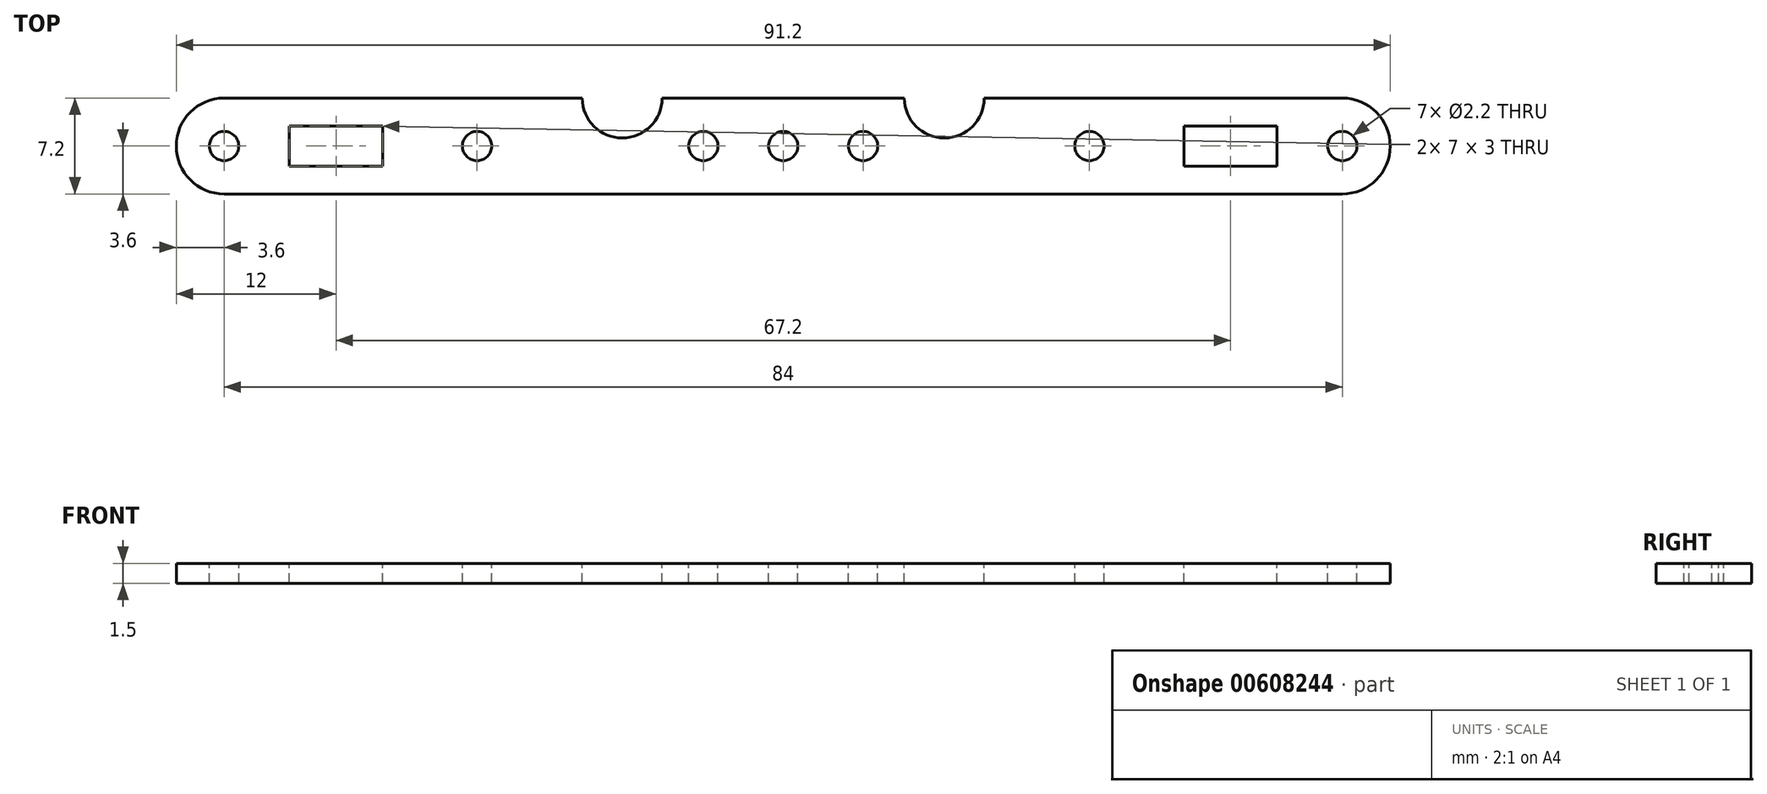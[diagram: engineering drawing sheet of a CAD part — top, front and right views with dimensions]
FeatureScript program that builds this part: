
annotation { "Feature Type Name" : "Feature", "Feature Type Description" : "" }
export const myFeature = defineFeature(function(context is Context, id is Id, definition is map)
    precondition{}
    {
        {
            var Q0;
            Q0=qCreatedBy(makeId("Top.planeOp"),FACE);
            var sketch = newSketch(context, id + "F0", { "sketchPlane" : qUnion([Q0])});
            skLineSegment(sketch, "E0", {"start": v(-56.58, 0) * mm, "end": v(51.41, 0) * mm, "construction": true});
            skLineSegment(sketch, "E1", {"start": v(0, 12.54) * mm, "end": v(0, -15.45) * mm, "construction": true});
            skLineSegment(sketch, "E2", {"start": v(-42, 3.6) * mm, "end": v(42, 3.6) * mm});
            skLineSegment(sketch, "E3", {"start": v(-42, -3.6) * mm, "end": v(42, -3.6) * mm});
            skArc(sketch, "E4", {"start": v(-42, 3.6) * mm, "mid": v(-45.6, 0) * mm, "end": v(-42, -3.6) * mm});
            skArc(sketch, "E5", {"start": v(42, -3.6) * mm, "mid": v(45.6, 0) * mm, "end": v(42, 3.6) * mm});
            skPoint(sketch, "E6", {"position": v(0, -3.6) * mm});
            skSolve(sketch);
        }
        {
            var Q0;
            Q0=makeQuery(id+"F0.imprint","IMPRINT",FACE,{"disambiguationData":[TD([[makeQuery(id+"F0.imprint","IMPRINT",EDGE,{"derivedFrom":sQuery(id+"F0.wireOp",EDGE,"E2")}),-1.0]])]});
            extrude(context, id + "F1", {"entities" : qUnion([Q0]), "depth" : 1.5 * mm, "offsetDistance" : 25 * mm});
        }
        {
            var Q0;
            Q0=makeQuery(id+"F1.opExtrude","CAP_FACE",FACE,{"disambiguationData":[OSD([sQuery(id+"F0.wireOp",EDGE,"E2"),sQuery(id+"F0.wireOp",EDGE,"E3"),sQuery(id+"F0.wireOp",EDGE,"E4"),sQuery(id+"F0.wireOp",EDGE,"E5")])],"isStart":false});
            var sketch = newSketch(context, id + "F2", { "sketchPlane" : qUnion([Q0])});
            skLineSegment(sketch, "E7", {"start": v(-42, 0) * mm, "end": v(42, 0) * mm, "construction": true});
            skCircle(sketch, "E8", {"center": v(-42, 0) * mm, "radius": 1.1 * mm});
            skCircle(sketch, "E9", {"center": v(42, 0) * mm, "radius": 1.1 * mm});
            skCircle(sketch, "E10", {"center": v(0, 0) * mm, "radius": 1.1 * mm});
            skCircle(sketch, "E11", {"center": v(-36, 0) * mm, "radius": 1.1 * mm});
            skCircle(sketch, "E12", {"center": v(36, 0) * mm, "radius": 1.1 * mm});
            skCircle(sketch, "E13", {"center": v(-23, 0) * mm, "radius": 1.1 * mm});
            skCircle(sketch, "E14", {"center": v(23, 0) * mm, "radius": 1.1 * mm});
            skCircle(sketch, "E15", {"center": v(-6, 0) * mm, "radius": 1.1 * mm});
            skCircle(sketch, "E16", {"center": v(6, 0) * mm, "radius": 1.1 * mm});
            skSolve(sketch);
        }
        {
            var Q0;
            Q0 = qSketchRegion(id + "F2", true);
            extrude(context, id + "F3", {"entities" : qUnion([Q0]), "operationType" : NewBodyOperationType.REMOVE, "endBound" : BoundingType.THROUGH_ALL, "oppositeDirection" : true, "depth" : 25 * mm, "offsetDistance" : 25 * mm});
        }
        {
            var Q0;
            Q0=makeQuery(id+"F1.opExtrude","CAP_FACE",FACE,{"disambiguationData":[OSD([sQuery(id+"F0.wireOp",EDGE,"E2"),sQuery(id+"F0.wireOp",EDGE,"E3"),sQuery(id+"F0.wireOp",EDGE,"E4"),sQuery(id+"F0.wireOp",EDGE,"E5")])],"isStart":false});
            var sketch = newSketch(context, id + "F4", { "sketchPlane" : qUnion([Q0])});
            skLineSegment(sketch, "E17.bottom", {"start": v(-37.1, 1.5) * mm, "end": v(-30.1, 1.5) * mm});
            skLineSegment(sketch, "E17.top", {"start": v(-37.1, -1.5) * mm, "end": v(-30.1, -1.5) * mm});
            skLineSegment(sketch, "E17.left", {"start": v(-37.1, 1.5) * mm, "end": v(-37.1, -1.5) * mm});
            skLineSegment(sketch, "E17.right", {"start": v(-30.1, 1.5) * mm, "end": v(-30.1, -1.5) * mm});
            skLineSegment(sketch, "E18", {"start": v(-30.1, 0) * mm, "end": v(-32.83, 0) * mm, "construction": true});
            skPoint(sketch, "E18.startSnap0", {"position": v(-30.1, 0) * mm});
            skPoint(sketch, "E18.endSnap0", {"position": v(-30.1, 0) * mm});
            skCircle(sketch, "E19", {"center": v(-12.1, 3.6) * mm, "radius": 3 * mm});
            skLineSegment(sketch, "E20", {"start": v(0, 7.35) * mm, "end": v(0, -7.75) * mm, "construction": true});
            skPoint(sketch, "E20.endSnap0", {"position": v(0, -3.6) * mm});
            skLineSegment(sketch, "E21.MirrorCS", {"start": v(30.1, 1.5) * mm, "end": v(30.1, -1.5) * mm});
            skPoint(sketch, "E22.MirrorP", {"position": v(30.1, 0) * mm});
            skLineSegment(sketch, "E23.MirrorCS", {"start": v(30.1, 0) * mm, "end": v(32.83, 0) * mm, "construction": true});
            skCircle(sketch, "E24.MirrorC", {"center": v(12.1, 3.6) * mm, "radius": 3 * mm});
            skLineSegment(sketch, "E25.MirrorCS", {"start": v(37.1, 1.5) * mm, "end": v(37.1, -1.5) * mm});
            skLineSegment(sketch, "E26.MirrorCS", {"start": v(37.1, -1.5) * mm, "end": v(30.1, -1.5) * mm});
            skLineSegment(sketch, "E27.MirrorCS", {"start": v(37.1, 1.5) * mm, "end": v(30.1, 1.5) * mm});
            skSolve(sketch);
        }
        {
            var Q0;
            Q0 = qSketchRegion(id + "F4", true);
            extrude(context, id + "F5", {"entities" : qUnion([Q0]), "operationType" : NewBodyOperationType.REMOVE, "endBound" : BoundingType.THROUGH_ALL, "oppositeDirection" : true, "depth" : 25 * mm, "offsetDistance" : 25 * mm});
        }
    });
